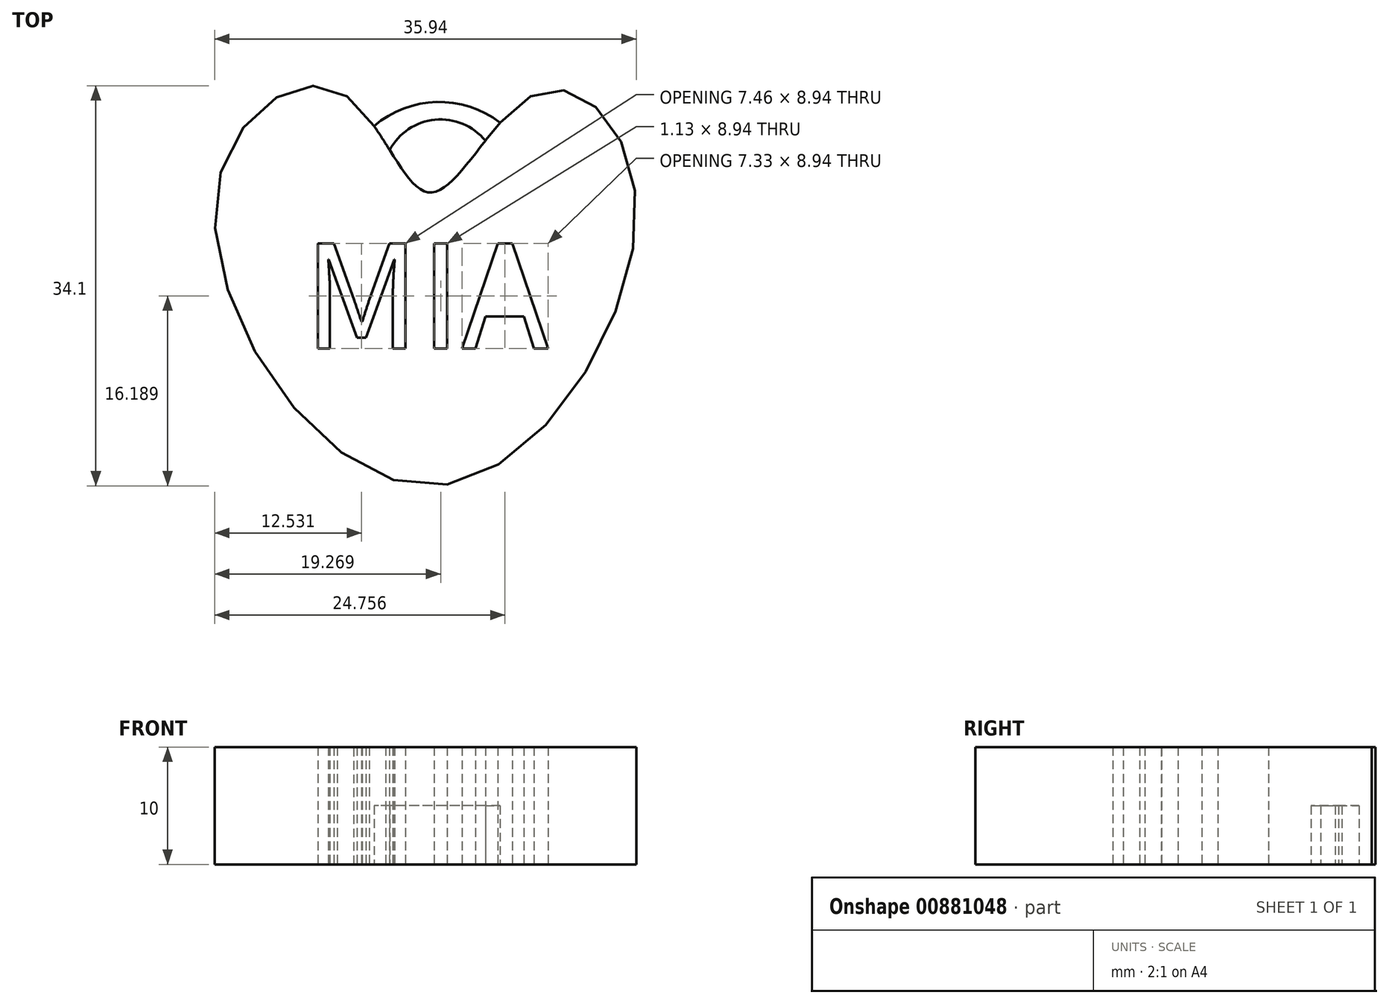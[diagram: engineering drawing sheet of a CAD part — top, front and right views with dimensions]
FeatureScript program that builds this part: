
annotation { "Feature Type Name" : "Feature", "Feature Type Description" : "" }
export const myFeature = defineFeature(function(context is Context, id is Id, definition is map)
    precondition{}
    {
        {
            var Q0;
            Q0=qCreatedBy(makeId("Top.planeOp"),FACE);
            var sketch = newSketch(context, id + "F0", { "sketchPlane" : qUnion([Q0])});
            skFitSpline(sketch, "E0", {"points": [v(0, 19.83) * mm, v(-7.86, 28.5) * mm, v(-18.25, 19.46) * mm, v(0, -5.17) * mm, v(17.56, 19.23) * mm, v(9.2, 28.33) * mm, v(0, 19.83) * mm]});
            skText(sketch, "E1", { "text": "MIA", "fontName": "NotoSansCJKkr-Regular.otf"});
            skArc(sketch, "E2", {"start": v(6, 25.78) * mm, "mid": v(0.57, 27.55) * mm, "end": v(-4.76, 25.5) * mm});
            skArc(sketch, "E3", {"start": v(4.73, 24.25) * mm, "mid": v(0.44, 26.04) * mm, "end": v(-3.43, 23.45) * mm});
            const initialGuessF0  = {"E1": [-0.01077, 0.00655, 1, 0, 0.00878]};
            skSetInitialGuess(sketch, initialGuessF0);
            skSolve(sketch);
        }
        {
            var Q0;
            Q0=makeQuery(id+"F0.imprint","IMPRINT",FACE,{"disambiguationData":[TD([[makeQuery(id+"F0.imprint","IMPRINT",EDGE,{"derivedFrom":sQuery(id+"F0.wireOp",EDGE,"E0")}),1.0]])]});
            extrude(context, id + "F1", {"entities" : qUnion([Q0]), "depth" : 5 * mm, "offsetDistance" : 25.4 * mm});
        }
        {
            var Q0;
            Q0=makeQuery(id+"F1.opExtrude","CAP_FACE",FACE,{"disambiguationData":[OSD([sQuery(id+"F0.wireOp",EDGE,"E0"),sQuery(id+"F0.wireOp",EDGE,"E1.sketch_text.stroke-0"),sQuery(id+"F0.wireOp",EDGE,"E1.sketch_text.stroke-1"),sQuery(id+"F0.wireOp",EDGE,"E1.sketch_text.stroke-2"),sQuery(id+"F0.wireOp",EDGE,"E1.sketch_text.stroke-3"),sQuery(id+"F0.wireOp",EDGE,"E1.sketch_text.stroke-4"),sQuery(id+"F0.wireOp",EDGE,"E1.sketch_text.stroke-5"),sQuery(id+"F0.wireOp",EDGE,"E1.sketch_text.stroke-6"),sQuery(id+"F0.wireOp",EDGE,"E1.sketch_text.stroke-7"),sQuery(id+"F0.wireOp",EDGE,"E1.sketch_text.stroke-8"),sQuery(id+"F0.wireOp",EDGE,"E1.sketch_text.stroke-9"),sQuery(id+"F0.wireOp",EDGE,"E1.sketch_text.stroke-10"),sQuery(id+"F0.wireOp",EDGE,"E1.sketch_text.stroke-11"),sQuery(id+"F0.wireOp",EDGE,"E1.sketch_text.stroke-12"),sQuery(id+"F0.wireOp",EDGE,"E1.sketch_text.stroke-13"),sQuery(id+"F0.wireOp",EDGE,"E1.sketch_text.stroke-14"),sQuery(id+"F0.wireOp",EDGE,"E1.sketch_text.stroke-15"),sQuery(id+"F0.wireOp",EDGE,"E1.sketch_text.stroke-16"),sQuery(id+"F0.wireOp",EDGE,"E1.sketch_text.stroke-17"),sQuery(id+"F0.wireOp",EDGE,"E1.sketch_text.stroke-18"),sQuery(id+"F0.wireOp",EDGE,"E1.sketch_text.stroke-19"),sQuery(id+"F0.wireOp",EDGE,"E1.sketch_text.stroke-20"),sQuery(id+"F0.wireOp",EDGE,"E1.sketch_text.stroke-21"),sQuery(id+"F0.wireOp",EDGE,"E1.sketch_text.stroke-22"),sQuery(id+"F0.wireOp",EDGE,"E1.sketch_text.stroke-23"),sQuery(id+"F0.wireOp",EDGE,"E1.sketch_text.stroke-24"),sQuery(id+"F0.wireOp",EDGE,"E1.sketch_text.stroke-25"),sQuery(id+"F0.wireOp",EDGE,"E1.sketch_text.stroke-32"),sQuery(id+"F0.wireOp",EDGE,"E1.sketch_text.stroke-33"),sQuery(id+"F0.wireOp",EDGE,"E1.sketch_text.stroke-34"),sQuery(id+"F0.wireOp",EDGE,"E1.sketch_text.stroke-35"),sQuery(id+"F0.wireOp",EDGE,"E1.sketch_text.stroke-36"),sQuery(id+"F0.wireOp",EDGE,"E1.sketch_text.stroke-37"),sQuery(id+"F0.wireOp",EDGE,"E1.sketch_text.stroke-38"),sQuery(id+"F0.wireOp",EDGE,"E1.sketch_text.stroke-39")])],"isStart":false});
            var Q1;
            Q1=makeQuery(id+"F0.imprint","IMPRINT",FACE,{"disambiguationData":[TD([[makeQuery(id+"F0.imprint","IMPRINT",EDGE,{"derivedFrom":sQuery(id+"F0.wireOp",EDGE,"E1.sketch_text.stroke-0")}),-1.0]])]});
            var Q2;
            Q2=makeQuery(id+"F1.opExtrude","CAP_FACE",FACE,{"disambiguationData":[OSD([sQuery(id+"F0.wireOp",EDGE,"E0"),sQuery(id+"F0.wireOp",EDGE,"E1.sketch_text.stroke-0"),sQuery(id+"F0.wireOp",EDGE,"E1.sketch_text.stroke-1"),sQuery(id+"F0.wireOp",EDGE,"E1.sketch_text.stroke-2"),sQuery(id+"F0.wireOp",EDGE,"E1.sketch_text.stroke-3"),sQuery(id+"F0.wireOp",EDGE,"E1.sketch_text.stroke-4"),sQuery(id+"F0.wireOp",EDGE,"E1.sketch_text.stroke-5"),sQuery(id+"F0.wireOp",EDGE,"E1.sketch_text.stroke-6"),sQuery(id+"F0.wireOp",EDGE,"E1.sketch_text.stroke-7"),sQuery(id+"F0.wireOp",EDGE,"E1.sketch_text.stroke-8"),sQuery(id+"F0.wireOp",EDGE,"E1.sketch_text.stroke-9"),sQuery(id+"F0.wireOp",EDGE,"E1.sketch_text.stroke-10"),sQuery(id+"F0.wireOp",EDGE,"E1.sketch_text.stroke-11"),sQuery(id+"F0.wireOp",EDGE,"E1.sketch_text.stroke-12"),sQuery(id+"F0.wireOp",EDGE,"E1.sketch_text.stroke-13"),sQuery(id+"F0.wireOp",EDGE,"E1.sketch_text.stroke-14"),sQuery(id+"F0.wireOp",EDGE,"E1.sketch_text.stroke-15"),sQuery(id+"F0.wireOp",EDGE,"E1.sketch_text.stroke-16"),sQuery(id+"F0.wireOp",EDGE,"E1.sketch_text.stroke-17"),sQuery(id+"F0.wireOp",EDGE,"E1.sketch_text.stroke-18"),sQuery(id+"F0.wireOp",EDGE,"E1.sketch_text.stroke-19"),sQuery(id+"F0.wireOp",EDGE,"E1.sketch_text.stroke-20"),sQuery(id+"F0.wireOp",EDGE,"E1.sketch_text.stroke-21"),sQuery(id+"F0.wireOp",EDGE,"E1.sketch_text.stroke-22"),sQuery(id+"F0.wireOp",EDGE,"E1.sketch_text.stroke-23"),sQuery(id+"F0.wireOp",EDGE,"E1.sketch_text.stroke-24"),sQuery(id+"F0.wireOp",EDGE,"E1.sketch_text.stroke-25"),sQuery(id+"F0.wireOp",EDGE,"E1.sketch_text.stroke-32"),sQuery(id+"F0.wireOp",EDGE,"E1.sketch_text.stroke-33"),sQuery(id+"F0.wireOp",EDGE,"E1.sketch_text.stroke-34"),sQuery(id+"F0.wireOp",EDGE,"E1.sketch_text.stroke-35"),sQuery(id+"F0.wireOp",EDGE,"E1.sketch_text.stroke-36"),sQuery(id+"F0.wireOp",EDGE,"E1.sketch_text.stroke-37"),sQuery(id+"F0.wireOp",EDGE,"E1.sketch_text.stroke-38"),sQuery(id+"F0.wireOp",EDGE,"E1.sketch_text.stroke-39")])],"isStart":true});
            var Q3;
            {var subQ0=sQuery(id+"F0.wireOp",EDGE,"E2");Q3=makeQuery(id+"F0.imprint","IMPRINT",FACE,{"disambiguationData":[TD([[makeQuery(id+"F0.imprint","IMPRINT",EDGE,{"derivedFrom":subQ0}),1.0]])]});}
            extrude(context, id + "F2", {"entities" : qUnion([Q0, Q1, Q2, Q3]), "operationType" : NewBodyOperationType.ADD, "depth" : 5 * mm, "offsetDistance" : 25.4 * mm});
        }
    });
